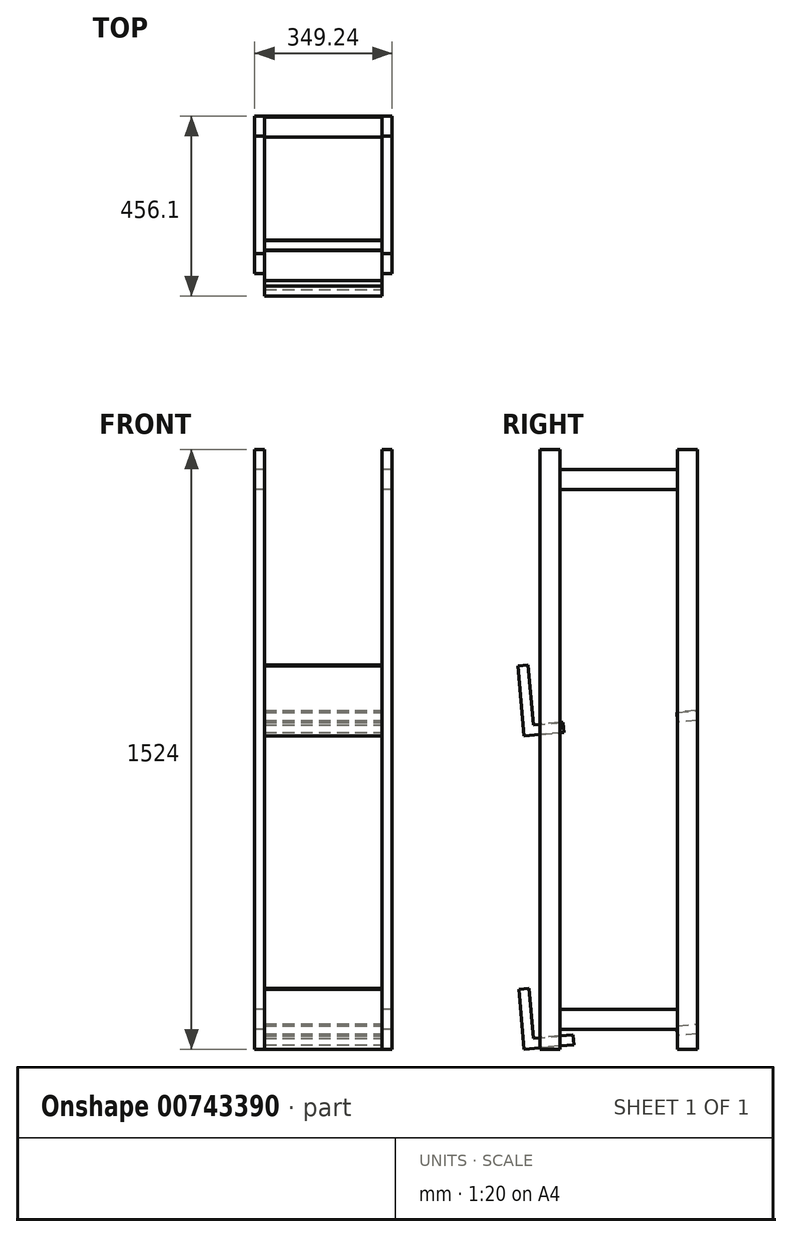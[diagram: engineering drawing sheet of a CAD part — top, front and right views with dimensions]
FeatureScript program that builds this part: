
annotation { "Feature Type Name" : "Feature", "Feature Type Description" : "" }
export const myFeature = defineFeature(function(context is Context, id is Id, definition is map)
    precondition{}
    {
        {
            var Q0;
            Q0=qCreatedBy(makeId("Top.planeOp"),FACE);
            var sketch = newSketch(context, id + "F0", { "sketchPlane" : qUnion([Q0])});
            skLineSegment(sketch, "E0.bottom", {"start": v(-174.62, 200.03) * mm, "end": v(174.63, 200.03) * mm, "construction": true});
            skLineSegment(sketch, "E0.top", {"start": v(-174.63, -200.03) * mm, "end": v(174.62, -200.03) * mm, "construction": true});
            skLineSegment(sketch, "E0.left", {"start": v(-174.62, 200.03) * mm, "end": v(-174.63, -200.03) * mm, "construction": true});
            skLineSegment(sketch, "E0.right", {"start": v(174.63, 200.03) * mm, "end": v(174.62, -200.03) * mm, "construction": true});
            skPoint(sketch, "E0.middle", {"position": v(0, 0) * mm});
            skLineSegment(sketch, "E1.bottom", {"start": v(-174.62, 200.03) * mm, "end": v(-149.23, 200.03) * mm});
            skLineSegment(sketch, "E1.top", {"start": v(-174.63, 149.22) * mm, "end": v(-149.23, 149.22) * mm});
            skLineSegment(sketch, "E1.left", {"start": v(-174.62, 200.03) * mm, "end": v(-174.62, 149.22) * mm});
            skLineSegment(sketch, "E1.right", {"start": v(-149.22, 200.03) * mm, "end": v(-149.22, 149.22) * mm});
            skPoint(sketch, "E1.middle", {"position": v(-161.93, 174.62) * mm});
            skLineSegment(sketch, "E2.bottom", {"start": v(149.23, 200.03) * mm, "end": v(174.63, 200.03) * mm});
            skLineSegment(sketch, "E2.top", {"start": v(149.23, 149.22) * mm, "end": v(174.63, 149.22) * mm});
            skLineSegment(sketch, "E2.left", {"start": v(149.23, 200.03) * mm, "end": v(149.23, 149.22) * mm});
            skLineSegment(sketch, "E2.right", {"start": v(174.63, 200.03) * mm, "end": v(174.63, 149.22) * mm});
            skPoint(sketch, "E2.middle", {"position": v(161.93, 174.63) * mm});
            skLineSegment(sketch, "E3.bottom", {"start": v(149.22, -149.22) * mm, "end": v(174.62, -149.22) * mm});
            skLineSegment(sketch, "E3.top", {"start": v(149.22, -200.03) * mm, "end": v(174.62, -200.03) * mm});
            skLineSegment(sketch, "E3.left", {"start": v(149.22, -149.22) * mm, "end": v(149.22, -200.03) * mm});
            skLineSegment(sketch, "E3.right", {"start": v(174.62, -149.22) * mm, "end": v(174.62, -200.03) * mm});
            skPoint(sketch, "E3.middle", {"position": v(161.92, -174.62) * mm});
            skLineSegment(sketch, "E4.bottom", {"start": v(-174.63, -149.22) * mm, "end": v(-149.23, -149.22) * mm});
            skLineSegment(sketch, "E4.top", {"start": v(-174.63, -200.03) * mm, "end": v(-149.23, -200.03) * mm});
            skLineSegment(sketch, "E4.left", {"start": v(-174.62, -149.22) * mm, "end": v(-174.62, -200.03) * mm});
            skLineSegment(sketch, "E4.right", {"start": v(-149.22, -149.22) * mm, "end": v(-149.22, -200.03) * mm});
            skPoint(sketch, "E4.middle", {"position": v(-161.93, -174.62) * mm});
            skSolve(sketch);
        }
        {
            var Q0;
            Q0 = qSketchRegion(id + "F0", true);
            extrude(context, id + "F1", {"entities" : qUnion([Q0]), "depth" : 1524 * mm, "offsetDistance" : 25.4 * mm});
        }
        {
            var Q0;
            Q0=makeQuery(id+"F1.opExtrude","SWEPT_FACE",FACE,{"disambiguationData":[OSD([sQuery(id+"F0.wireOp",EDGE,"E2.top")])]});
            var sketch = newSketch(context, id + "F2", { "sketchPlane" : qUnion([Q0])});
            skLineSegment(sketch, "E5.bottom", {"start": v(149.23, 1473.2) * mm, "end": v(174.63, 1473.2) * mm});
            skLineSegment(sketch, "E5.top", {"start": v(149.23, 1422.4) * mm, "end": v(174.63, 1422.4) * mm});
            skLineSegment(sketch, "E5.left", {"start": v(149.23, 1473.2) * mm, "end": v(149.23, 1422.4) * mm});
            skLineSegment(sketch, "E5.right", {"start": v(174.63, 1473.2) * mm, "end": v(174.63, 1422.4) * mm});
            skPoint(sketch, "E6.oppositeSnap0", {"position": v(161.93, 1422.4) * mm});
            skLineSegment(sketch, "E6.bottom", {"start": v(-174.63, 1473.2) * mm, "end": v(-149.23, 1473.2) * mm});
            skLineSegment(sketch, "E6.top", {"start": v(-174.63, 1422.4) * mm, "end": v(-149.23, 1422.4) * mm});
            skLineSegment(sketch, "E6.left", {"start": v(-174.63, 1473.2) * mm, "end": v(-174.63, 1422.4) * mm});
            skLineSegment(sketch, "E6.right", {"start": v(-149.23, 1473.2) * mm, "end": v(-149.23, 1422.4) * mm});
            skLineSegment(sketch, "E7.bottom", {"start": v(149.23, 101.6) * mm, "end": v(174.63, 101.6) * mm});
            skLineSegment(sketch, "E7.top", {"start": v(149.23, 50.8) * mm, "end": v(174.63, 50.8) * mm});
            skLineSegment(sketch, "E7.left", {"start": v(149.23, 101.6) * mm, "end": v(149.23, 50.8) * mm});
            skLineSegment(sketch, "E7.right", {"start": v(174.63, 101.6) * mm, "end": v(174.63, 50.8) * mm});
            skLineSegment(sketch, "E8.bottom", {"start": v(-174.63, 101.6) * mm, "end": v(-149.23, 101.6) * mm});
            skLineSegment(sketch, "E8.top", {"start": v(-174.63, 50.8) * mm, "end": v(-149.23, 50.8) * mm});
            skLineSegment(sketch, "E8.left", {"start": v(-174.63, 101.6) * mm, "end": v(-174.63, 50.8) * mm});
            skLineSegment(sketch, "E8.right", {"start": v(-149.23, 101.6) * mm, "end": v(-149.23, 50.8) * mm});
            skSolve(sketch);
        }
        {
            var Q0;
            Q0 = qSketchRegion(id + "F2", true);
            extrude(context, id + "F3", {"entities" : qUnion([Q0]), "endBound" : BoundingType.UP_TO_NEXT, "depth" : 25.4 * mm, "offsetDistance" : 25.4 * mm});
        }
        {
            var Q0;
            Q0=makeQuery(id+"F1.opExtrude","SWEPT_FACE",FACE,{"disambiguationData":[OSD([sQuery(id+"F0.wireOp",EDGE,"E3.left")])]});
            var sketch = newSketch(context, id + "F4", { "sketchPlane" : qUnion([Q0])});
            skLineSegment(sketch, "E9", {"start": v(217.48, 27.52) * mm, "end": v(266.18, 584.2) * mm});
            skLineSegment(sketch, "E10", {"start": v(266.18, 584.2) * mm, "end": v(-151.32, 620.72) * mm});
            skLineSegment(sketch, "E11", {"start": v(-151.32, 620.72) * mm, "end": v(-200.03, 64.04) * mm});
            skLineSegment(sketch, "E12", {"start": v(-200.03, 64.04) * mm, "end": v(217.48, 27.52) * mm});
            skLineSegment(sketch, "E13", {"start": v(-200.03, 860.44) * mm, "end": v(217.48, 823.92) * mm});
            skLineSegment(sketch, "E14", {"start": v(217.48, 823.92) * mm, "end": v(266.18, 1380.6) * mm});
            skLineSegment(sketch, "E15", {"start": v(266.18, 1380.6) * mm, "end": v(-151.32, 1417.12) * mm});
            skLineSegment(sketch, "E16", {"start": v(-151.32, 1417.12) * mm, "end": v(-200.03, 860.44) * mm});
            skSolve(sketch);
        }
        {
            var Q0;
            {var subQ0=sQuery(id+"F0.wireOp",EDGE,"E3.left");Q0=makeQuery(id+"F4.imprint","IMPRINT",FACE,{"disambiguationData":[TD([[makeQuery(id+"F4.imprint","IMPRINT",EDGE,{"derivedFrom":makeQuery(id+"F1.opExtrude","CAP_EDGE",EDGE,{"disambiguationData":[OSD([subQ0])],"isStart":true})}),1.0]])]});}
            var sketch = newSketch(context, id + "F5", { "sketchPlane" : qUnion([Q0])});
            skLineSegment(sketch, "E17", {"start": v(-197.81, 860.25) * mm, "end": v(-147.2, 855.82) * mm});
            skLineSegment(sketch, "E18", {"start": v(-147.2, 855.82) * mm, "end": v(-149.42, 830.52) * mm});
            skLineSegment(sketch, "E19", {"start": v(-149.42, 830.52) * mm, "end": v(-200.03, 834.95) * mm});
            skLineSegment(sketch, "E20", {"start": v(-200.03, 834.95) * mm, "end": v(-197.81, 860.25) * mm});
            skLineSegment(sketch, "E21", {"start": v(141.57, 830.56) * mm, "end": v(242.78, 821.7) * mm});
            skLineSegment(sketch, "E22", {"start": v(242.78, 821.7) * mm, "end": v(240.57, 796.4) * mm});
            skLineSegment(sketch, "E23", {"start": v(240.57, 796.4) * mm, "end": v(139.36, 805.26) * mm});
            skLineSegment(sketch, "E24", {"start": v(139.36, 805.26) * mm, "end": v(141.57, 830.56) * mm});
            skLineSegment(sketch, "E25", {"start": v(217.48, 823.92) * mm, "end": v(230.76, 975.74) * mm});
            skLineSegment(sketch, "E26", {"start": v(230.76, 975.74) * mm, "end": v(256.07, 973.52) * mm});
            skLineSegment(sketch, "E27", {"start": v(256.07, 973.52) * mm, "end": v(242.78, 821.7) * mm});
            skLineSegment(sketch, "E28", {"start": v(217.48, 823.92) * mm, "end": v(242.78, 821.7) * mm});
            skLineSegment(sketch, "E29", {"start": v(116.27, 36.37) * mm, "end": v(217.48, 27.52) * mm});
            skLineSegment(sketch, "E30", {"start": v(217.48, 27.52) * mm, "end": v(215.27, 2.21) * mm});
            skLineSegment(sketch, "E31", {"start": v(215.27, 2.21) * mm, "end": v(114.05, 11.07) * mm});
            skLineSegment(sketch, "E32", {"start": v(114.05, 11.07) * mm, "end": v(116.27, 36.37) * mm});
            skLineSegment(sketch, "E33", {"start": v(215.27, 2.21) * mm, "end": v(228.55, 154.03) * mm});
            skLineSegment(sketch, "E34", {"start": v(228.55, 154.03) * mm, "end": v(253.85, 151.82) * mm});
            skLineSegment(sketch, "E35", {"start": v(215.27, 2.21) * mm, "end": v(240.57, 0) * mm});
            skLineSegment(sketch, "E36", {"start": v(240.57, 0) * mm, "end": v(253.85, 151.82) * mm});
            skLineSegment(sketch, "E37", {"start": v(-200.03, 38.55) * mm, "end": v(-197.81, 63.85) * mm});
            skLineSegment(sketch, "E38", {"start": v(-197.81, 63.85) * mm, "end": v(-147.2, 59.42) * mm});
            skLineSegment(sketch, "E39", {"start": v(-147.2, 59.42) * mm, "end": v(-149.42, 34.12) * mm});
            skLineSegment(sketch, "E40", {"start": v(-149.42, 34.12) * mm, "end": v(-200.03, 38.55) * mm});
            skSolve(sketch);
        }
        {
            var Q0;
            Q0 = qSketchRegion(id + "F5", true);
            var Q1;
            Q1=makeQuery(id+"F1.opExtrude","SWEPT_FACE",FACE,{"disambiguationData":[OSD([sQuery(id+"F0.wireOp",EDGE,"E1.right")])]});
            extrude(context, id + "F6", {"entities" : qUnion([Q0]), "endBound" : BoundingType.UP_TO_SURFACE, "depth" : 25.4 * mm, "endBoundEntityFace" : qUnion([Q1]), "offsetDistance" : 25.4 * mm});
        }
    });
